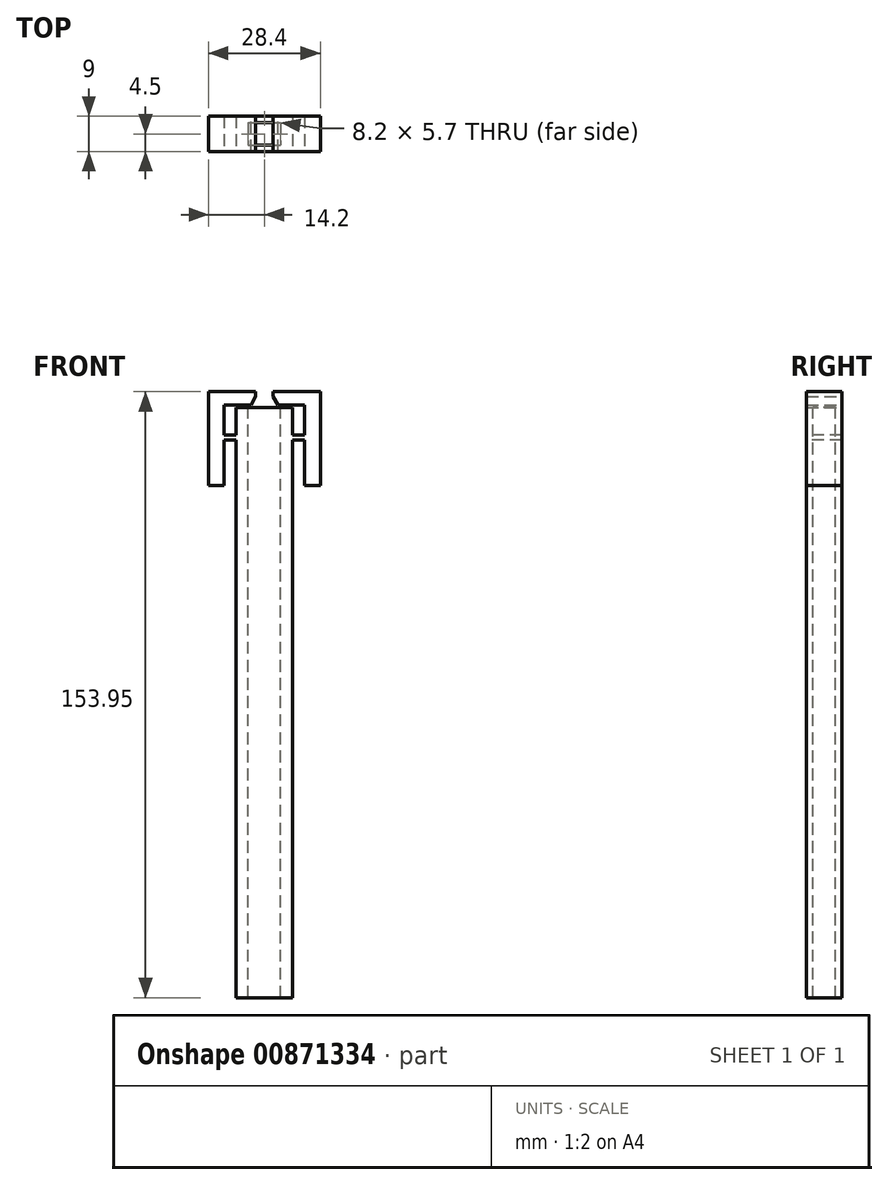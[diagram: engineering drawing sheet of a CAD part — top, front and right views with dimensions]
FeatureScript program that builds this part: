
annotation { "Feature Type Name" : "Feature", "Feature Type Description" : "" }
export const myFeature = defineFeature(function(context is Context, id is Id, definition is map)
    precondition{}
    {
        {
            var Q0;
            Q0=qCreatedBy(makeId("Front.planeOp"),FACE);
            var sketch = newSketch(context, id + "F0", { "sketchPlane" : qUnion([Q0])});
            skLineSegment(sketch, "E0.bottom", {"start": v(-7.2, 50) * mm, "end": v(7.2, 50) * mm});
            skLineSegment(sketch, "E0.top", {"start": v(-7.2, -50) * mm, "end": v(7.2, -50) * mm});
            skLineSegment(sketch, "E0.left", {"start": v(-7.2, 50) * mm, "end": v(-7.2, -50) * mm});
            skLineSegment(sketch, "E0.right", {"start": v(7.2, 50) * mm, "end": v(7.2, -50) * mm});
            skSolve(sketch);
        }
        {
            var Q0;
            Q0=makeQuery(id+"F0.imprint","IMPRINT",FACE,{"disambiguationData":[TD([[makeQuery(id+"F0.imprint","IMPRINT",EDGE,{"derivedFrom":sQuery(id+"F0.wireOp",EDGE,"E0.bottom")}),-1.0]])]});
            extrude(context, id + "F1", {"entities" : qUnion([Q0]), "endBound" : BoundingType.SYMMETRIC, "depth" : 9 * mm, "offsetDistance" : 25 * mm});
        }
        {
            var Q0;
            Q0=makeQuery(id+"F1.opExtrude","SWEPT_FACE",FACE,{"disambiguationData":[OSD([sQuery(id+"F0.wireOp",EDGE,"E0.bottom")])]});
            var sketch = newSketch(context, id + "F2", { "sketchPlane" : qUnion([Q0])});
            skLineSegment(sketch, "E1.bottom", {"start": v(-4.1, 2.85) * mm, "end": v(4.1, 2.85) * mm});
            skLineSegment(sketch, "E1.top", {"start": v(-4.1, -2.85) * mm, "end": v(4.1, -2.85) * mm});
            skLineSegment(sketch, "E1.left", {"start": v(-4.1, 2.85) * mm, "end": v(-4.1, -2.85) * mm});
            skLineSegment(sketch, "E1.right", {"start": v(4.1, 2.85) * mm, "end": v(4.1, -2.85) * mm});
            skSolve(sketch);
        }
        {
            var Q0;
            Q0=makeQuery(id+"F2.imprint","IMPRINT",FACE,{"disambiguationData":[TD([[makeQuery(id+"F2.imprint","IMPRINT",EDGE,{"derivedFrom":sQuery(id+"F2.wireOp",EDGE,"E1.bottom")}),-1.0]])]});
            extrude(context, id + "F3", {"entities" : qUnion([Q0]), "operationType" : NewBodyOperationType.REMOVE, "endBound" : BoundingType.THROUGH_ALL, "oppositeDirection" : true, "depth" : 25 * mm, "offsetDistance" : 25 * mm});
        }
        {
            var Q0;
            Q0=makeQuery(id+"F1.opExtrude","SWEPT_FACE",FACE,{"disambiguationData":[OSD([sQuery(id+"F0.wireOp",EDGE,"E0.left")])]});
            var sketch = newSketch(context, id + "F4", { "sketchPlane" : qUnion([Q0])});
            skLineSegment(sketch, "E2.bottom", {"start": v(-4.5, 43) * mm, "end": v(4.5, 43) * mm});
            skLineSegment(sketch, "E2.top", {"start": v(-4.5, 41.7) * mm, "end": v(4.5, 41.7) * mm});
            skLineSegment(sketch, "E2.left", {"start": v(-4.5, 43) * mm, "end": v(-4.5, 41.7) * mm});
            skLineSegment(sketch, "E2.right", {"start": v(4.5, 43) * mm, "end": v(4.5, 41.7) * mm});
            skSolve(sketch);
        }
        {
            var Q0;
            Q0=makeQuery(id+"F4.imprint","IMPRINT",FACE,{"disambiguationData":[TD([[makeQuery(id+"F4.imprint","IMPRINT",EDGE,{"derivedFrom":sQuery(id+"F4.wireOp",EDGE,"E2.bottom")}),-1.0]])]});
            extrude(context, id + "F5", {"entities" : qUnion([Q0]), "depth" : 6 * mm, "offsetDistance" : 25 * mm});
        }
        {
            var Q0;
            Q0=makeQuery(id+"F5.boolean.opBoolean","MERGE",FACE,{"derivedFrom":[makeQuery(id+"F1.opExtrude","CAP_FACE",FACE,{"disambiguationData":[OSD([sQuery(id+"F0.wireOp",EDGE,"E0.bottom"),sQuery(id+"F0.wireOp",EDGE,"E0.top"),sQuery(id+"F0.wireOp",EDGE,"E0.left"),sQuery(id+"F0.wireOp",EDGE,"E0.right")])],"isStart":true}),makeQuery(id+"F5.opExtrude","SWEPT_FACE",FACE,{"disambiguationData":[OSD([sQuery(id+"F4.wireOp",EDGE,"E2.left")])]})]});
            var sketch = newSketch(context, id + "F6", { "sketchPlane" : qUnion([Q0])});
            skLineSegment(sketch, "E3.bottom", {"start": v(10.2, 30.07) * mm, "end": v(14.2, 30.07) * mm});
            skLineSegment(sketch, "E3.top", {"start": v(10.2, 53.95) * mm, "end": v(14.2, 53.95) * mm});
            skLineSegment(sketch, "E3.left", {"start": v(10.2, 30.07) * mm, "end": v(10.2, 53.95) * mm});
            skLineSegment(sketch, "E3.right", {"start": v(14.2, 30.07) * mm, "end": v(14.2, 53.95) * mm});
            skLineSegment(sketch, "E4", {"start": v(10.2, 50.55) * mm, "end": v(3.4, 50.55) * mm});
            skLineSegment(sketch, "E5", {"start": v(3.4, 53.95) * mm, "end": v(10.2, 53.95) * mm});
            skLineSegment(sketch, "E6", {"start": v(3.4, 50.55) * mm, "end": v(2.2, 52.75) * mm});
            skLineSegment(sketch, "E7", {"start": v(2.2, 52.75) * mm, "end": v(2.2, 53.95) * mm});
            skLineSegment(sketch, "E8", {"start": v(2.2, 53.95) * mm, "end": v(3.4, 53.95) * mm});
            skSolve(sketch);
        }
        {
            var Q0;
            Q0 = qSketchRegion(id + "F6", true);
            extrude(context, id + "F7", {"entities" : qUnion([Q0]), "operationType" : NewBodyOperationType.ADD, "oppositeDirection" : true, "depth" : 9 * mm, "offsetDistance" : 25 * mm});
        }
        {
            var Q0;
            Q0=makeQuery(id+"F5.opExtrude","SWEPT_BODY",BODY,{"disambiguationData":[OSD([sQuery(id+"F4.wireOp",EDGE,"E2.bottom"),sQuery(id+"F4.wireOp",EDGE,"E2.top"),sQuery(id+"F4.wireOp",EDGE,"E2.left"),sQuery(id+"F4.wireOp",EDGE,"E2.right")])]});
            var Q1;
            Q1=makeQuery(id+"F7.opExtrude","SWEPT_BODY",BODY,{"disambiguationData":[OSD([sQuery(id+"F6.wireOp",EDGE,"E3.bottom"),sQuery(id+"F6.wireOp",EDGE,"E3.top"),sQuery(id+"F6.wireOp",EDGE,"E3.left"),sQuery(id+"F6.wireOp",EDGE,"E3.right"),sQuery(id+"F6.wireOp",EDGE,"E4"),sQuery(id+"F6.wireOp",EDGE,"E5"),sQuery(id+"F6.wireOp",EDGE,"E6"),sQuery(id+"F6.wireOp",EDGE,"E7"),sQuery(id+"F6.wireOp",EDGE,"E8")])]});
            var Q2;
            Q2=qCreatedBy(makeId("Right.planeOp"),FACE);
            mirror(context, id + "F8", {"operationType" : NewBodyOperationType.ADD, "entities" : qUnion([Q0, Q1]), "mirrorPlane" : qUnion([Q2])});
        }
        {
            var Q0;
            Q0=makeQuery(id+"F1.opExtrude","SWEPT_FACE",FACE,{"disambiguationData":[OSD([sQuery(id+"F0.wireOp",EDGE,"E0.top")])]});
            extrude(context, id + "F9", {"entities" : qUnion([Q0]), "operationType" : NewBodyOperationType.ADD, "depth" : 50 * mm, "offsetDistance" : 25 * mm});
        }
    });
